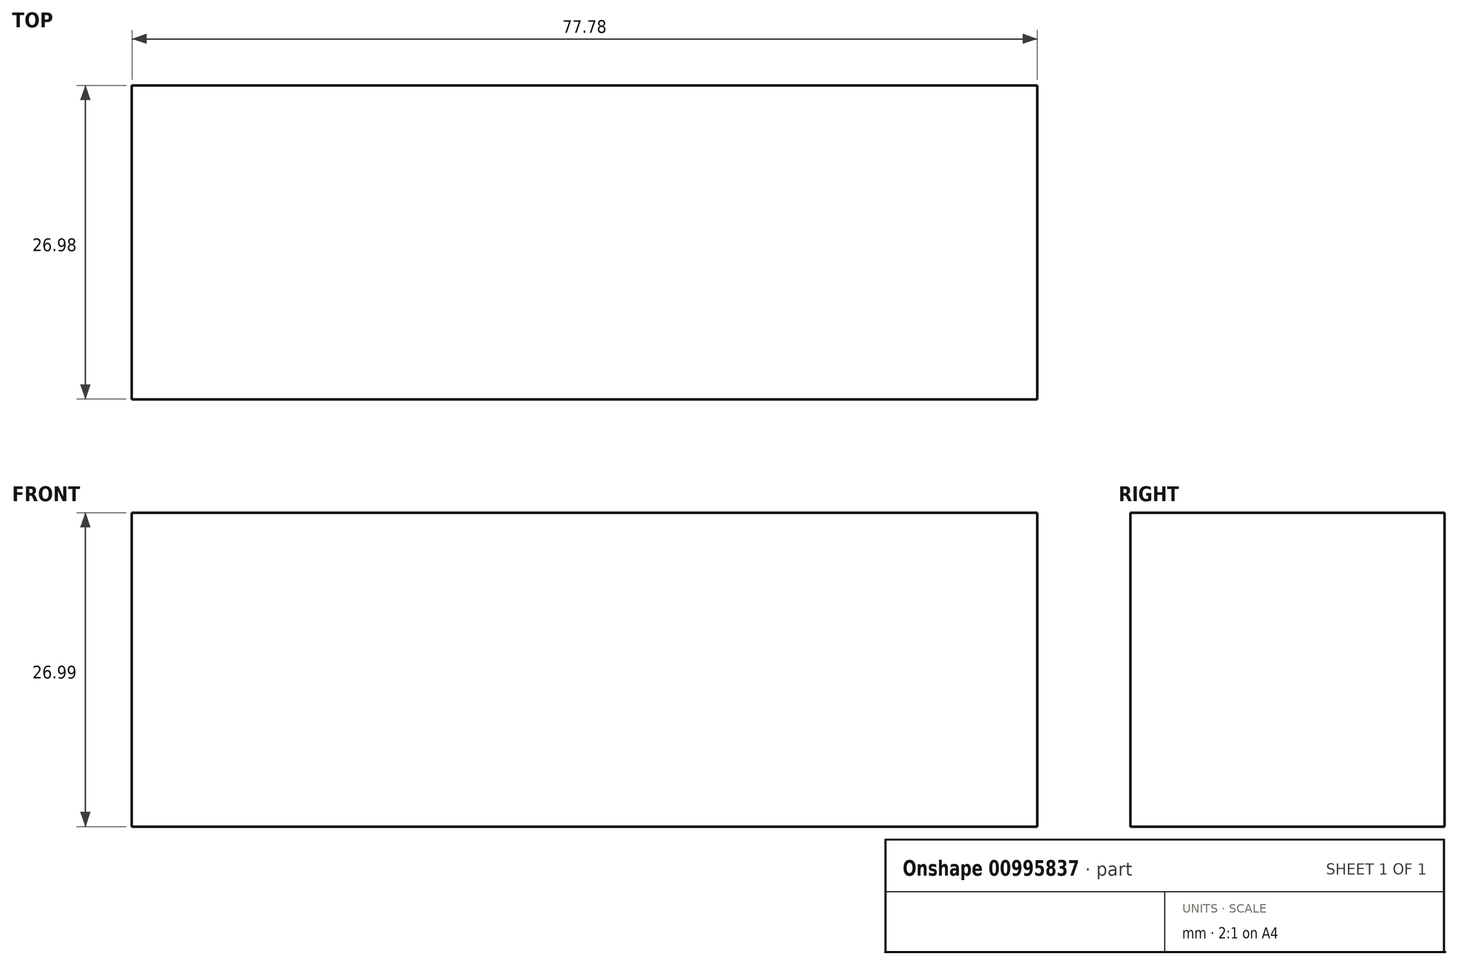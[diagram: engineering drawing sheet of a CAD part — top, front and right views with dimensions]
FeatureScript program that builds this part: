
annotation { "Feature Type Name" : "Feature", "Feature Type Description" : "" }
export const myFeature = defineFeature(function(context is Context, id is Id, definition is map)
    precondition{}
    {
        {
            var Q0;
            Q0=qCreatedBy(makeId("Top.planeOp"),FACE);
            var sketch = newSketch(context, id + "F0", { "sketchPlane" : qUnion([Q0])});
            skLineSegment(sketch, "E0.bottom", {"start": v(38.9, -13.5) * mm, "end": v(-38.9, -13.5) * mm});
            skLineSegment(sketch, "E0.top", {"start": v(38.9, 13.5) * mm, "end": v(-38.9, 13.5) * mm});
            skLineSegment(sketch, "E0.left", {"start": v(38.9, -13.5) * mm, "end": v(38.9, 13.5) * mm});
            skLineSegment(sketch, "E0.right", {"start": v(-38.9, -13.5) * mm, "end": v(-38.9, 13.5) * mm});
            skPoint(sketch, "E0.middle", {"position": v(0, 0) * mm});
            skSolve(sketch);
        }
        {
            var Q0;
            Q0 = qSketchRegion(id + "F0", true);
            extrude(context, id + "F1", {"entities" : qUnion([Q0]), "depth" : 26.99 * mm, "offsetDistance" : 25.4 * mm});
        }
    });
